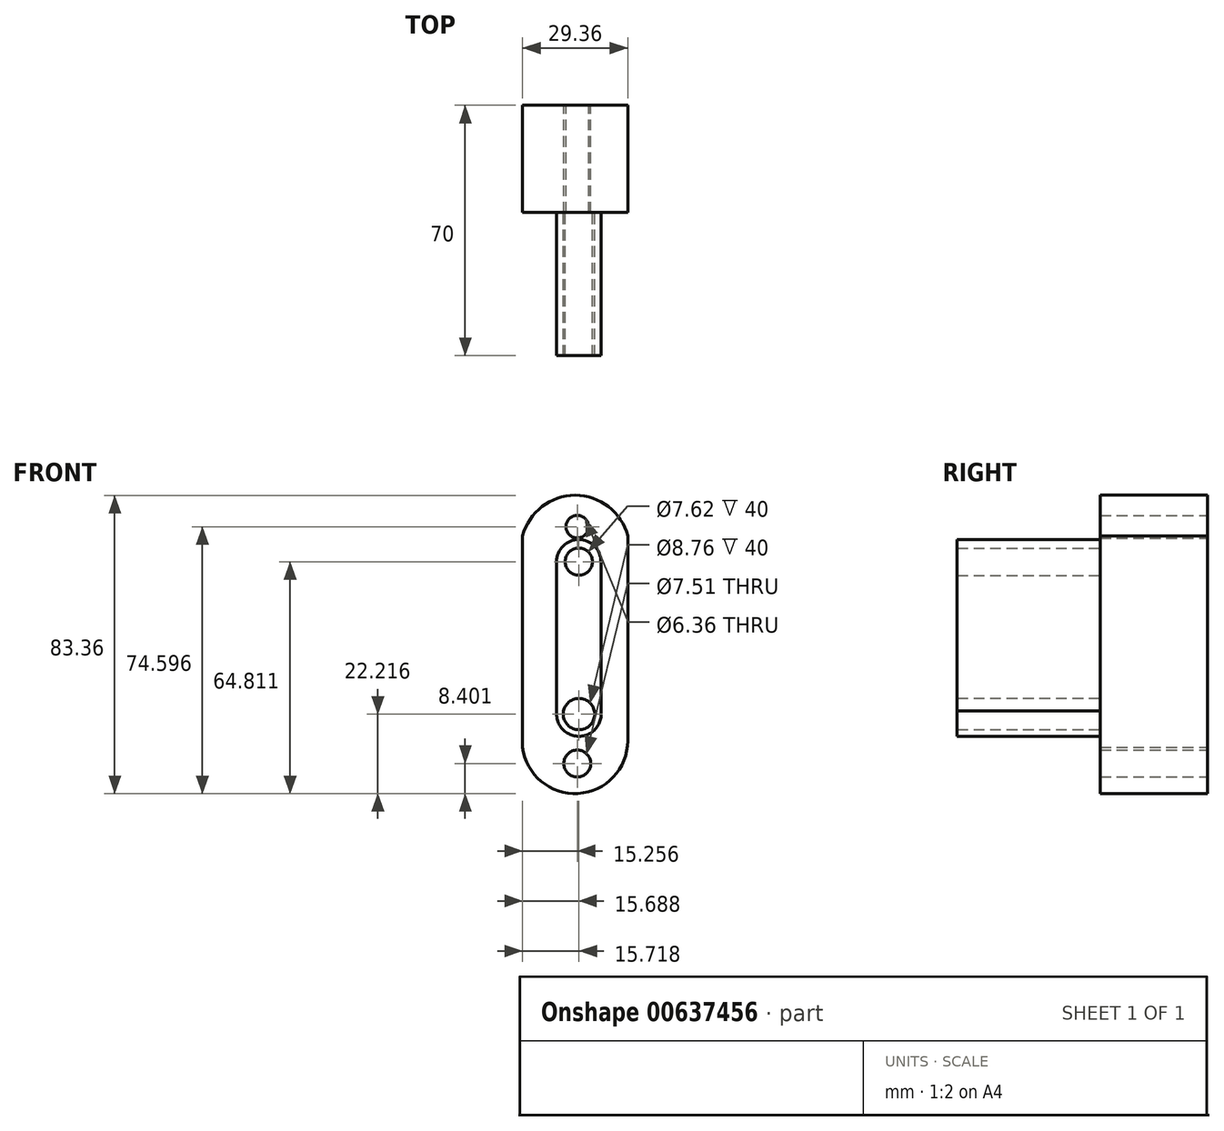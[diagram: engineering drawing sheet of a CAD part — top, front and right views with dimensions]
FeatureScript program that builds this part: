
annotation { "Feature Type Name" : "Feature", "Feature Type Description" : "" }
export const myFeature = defineFeature(function(context is Context, id is Id, definition is map)
    precondition{}
    {
        {
            var Q0;
            Q0=qCreatedBy(makeId("Front.planeOp"),FACE);
            var sketch = newSketch(context, id + "F0", { "sketchPlane" : qUnion([Q0])});
            skLineSegment(sketch, "E0", {"start": v(-17.99, 32.67) * mm, "end": v(-17.99, -26.33) * mm});
            skLineSegment(sketch, "E1", {"start": v(11.37, 32.67) * mm, "end": v(11.37, -24.6) * mm});
            skArc(sketch, "E2", {"start": v(11.37, 32.67) * mm, "mid": v(-3.3, 44.02) * mm, "end": v(-17.99, 32.67) * mm});
            skArc(sketch, "E3", {"start": v(-17.99, -26.33) * mm, "mid": v(-2.5, -39.31) * mm, "end": v(11.37, -24.6) * mm});
            skCircle(sketch, "E4", {"center": v(-2.73, 35.26) * mm, "radius": 3.18 * mm});
            skCircle(sketch, "E5", {"center": v(-2.73, -30.94) * mm, "radius": 3.75 * mm});
            skSolve(sketch);
        }
        {
            var Q0;
            Q0=qCreatedBy(makeId("Front.planeOp"),FACE);
            var sketch = newSketch(context, id + "F1", { "sketchPlane" : qUnion([Q0])});
            skLineSegment(sketch, "E6", {"start": v(-8.5, 25.47) * mm, "end": v(-8.5, -17.12) * mm});
            skLineSegment(sketch, "E7", {"start": v(3.89, 25.47) * mm, "end": v(3.89, -16.26) * mm});
            skArc(sketch, "E8", {"start": v(3.89, 25.47) * mm, "mid": v(-2.3, 31.66) * mm, "end": v(-8.5, 25.47) * mm});
            skArc(sketch, "E9", {"start": v(-8.5, -17.12) * mm, "mid": v(-1.84, -23.33) * mm, "end": v(3.89, -16.26) * mm});
            skCircle(sketch, "E10", {"center": v(-2.3, 25.47) * mm, "radius": 3.81 * mm});
            skCircle(sketch, "E11", {"center": v(-2.27, -17.12) * mm, "radius": 4.38 * mm});
            skSolve(sketch);
        }
        {
            var Q0;
            Q0 = qSketchRegion(id + "F1", true);
            extrude(context, id + "F2", {"entities" : qUnion([Q0]), "depth" : 70 * mm, "offsetDistance" : 25 * mm});
        }
        {
            var Q0;
            Q0 = qSketchRegion(id + "F0", true);
            extrude(context, id + "F3", {"entities" : qUnion([Q0]), "operationType" : NewBodyOperationType.ADD, "depth" : 30 * mm, "offsetDistance" : 25 * mm});
        }
    });
